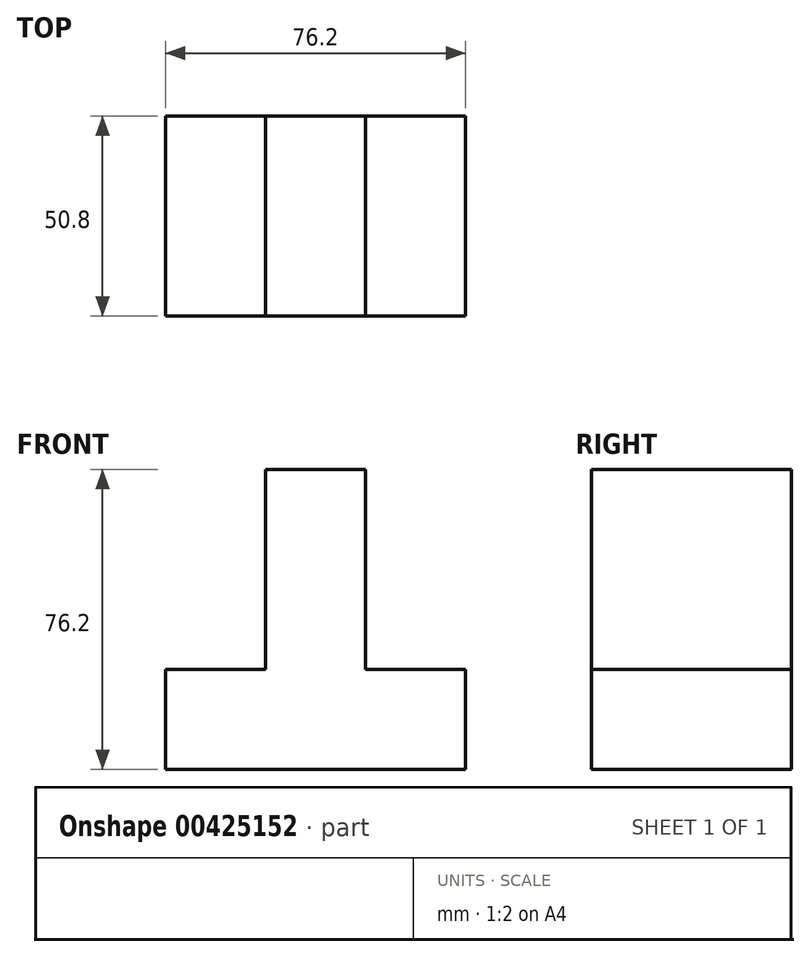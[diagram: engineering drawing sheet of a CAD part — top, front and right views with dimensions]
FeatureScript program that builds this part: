
annotation { "Feature Type Name" : "Feature", "Feature Type Description" : "" }
export const myFeature = defineFeature(function(context is Context, id is Id, definition is map)
    precondition{}
    {
        {
            var Q0;
            Q0=qCreatedBy(makeId("Front.planeOp"),FACE);
            var sketch = newSketch(context, id + "F0", { "sketchPlane" : qUnion([Q0])});
            skLineSegment(sketch, "E0", {"start": v(-33.23, 0) * mm, "end": v(42.97, 0) * mm});
            skLineSegment(sketch, "E1", {"start": v(42.97, 0) * mm, "end": v(42.97, 25.4) * mm});
            skLineSegment(sketch, "E2", {"start": v(42.97, 25.4) * mm, "end": v(17.57, 25.4) * mm});
            skLineSegment(sketch, "E3", {"start": v(17.57, 25.4) * mm, "end": v(17.57, 76.2) * mm});
            skLineSegment(sketch, "E4", {"start": v(17.57, 76.2) * mm, "end": v(-7.83, 76.2) * mm});
            skLineSegment(sketch, "E5", {"start": v(-7.83, 76.2) * mm, "end": v(-7.83, 25.4) * mm});
            skLineSegment(sketch, "E6", {"start": v(-7.83, 25.4) * mm, "end": v(-33.23, 25.4) * mm});
            skLineSegment(sketch, "E7", {"start": v(-33.23, 25.4) * mm, "end": v(-33.23, 0) * mm});
            skSolve(sketch);
        }
        {
            var Q0;
            Q0 = qSketchRegion(id + "F0", true);
            extrude(context, id + "F1", {"entities" : qUnion([Q0]), "depth" : 50.8 * mm});
        }
    });
